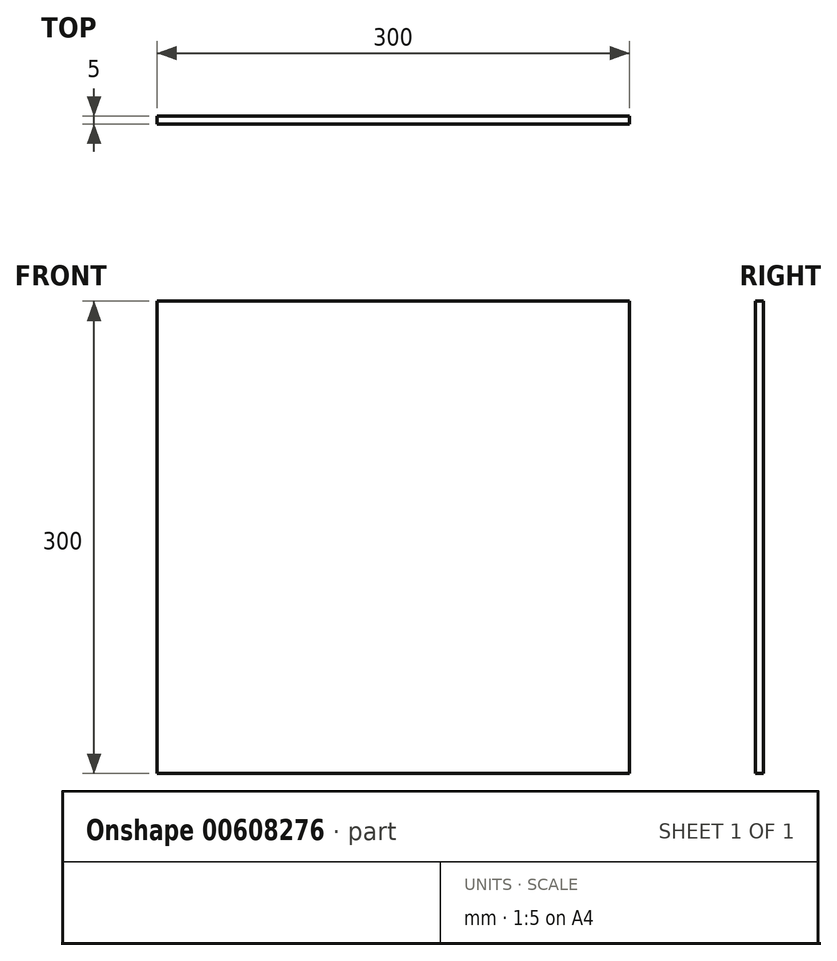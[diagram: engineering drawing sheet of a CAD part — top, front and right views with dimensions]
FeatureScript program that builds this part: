
annotation { "Feature Type Name" : "Feature", "Feature Type Description" : "" }
export const myFeature = defineFeature(function(context is Context, id is Id, definition is map)
    precondition{}
    {
        {
            var Q0;
            Q0=qCreatedBy(makeId("Front.planeOp"),FACE);
            var sketch = newSketch(context, id + "F0", { "sketchPlane" : qUnion([Q0])});
            skLineSegment(sketch, "E0.bottom", {"start": v(-150, 150) * mm, "end": v(150, 150) * mm});
            skLineSegment(sketch, "E0.top", {"start": v(-150, -150) * mm, "end": v(150, -150) * mm});
            skLineSegment(sketch, "E0.left", {"start": v(-150, 150) * mm, "end": v(-150, -150) * mm});
            skLineSegment(sketch, "E0.right", {"start": v(150, 150) * mm, "end": v(150, -150) * mm});
            skPoint(sketch, "E0.middle", {"position": v(0, 0) * mm});
            skSolve(sketch);
        }
        {
            var Q0;
            Q0 = qSketchRegion(id + "F0", true);
            extrude(context, id + "F1", {"entities" : qUnion([Q0]), "depth" : 5 * mm, "offsetDistance" : 25 * mm});
        }
    });
